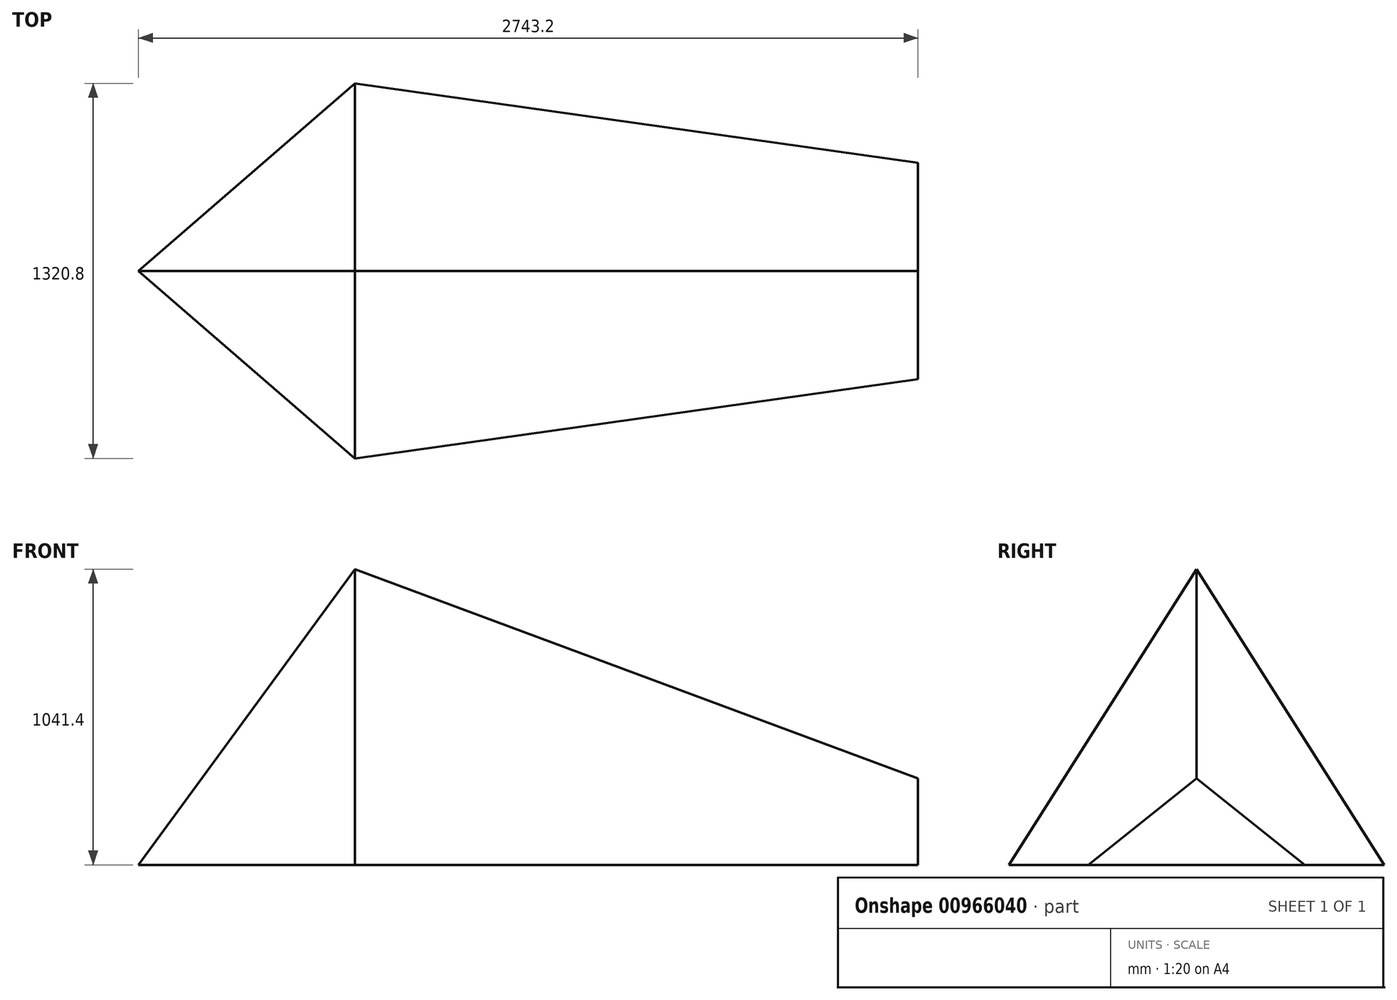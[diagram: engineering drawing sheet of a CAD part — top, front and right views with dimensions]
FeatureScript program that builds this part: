
annotation { "Feature Type Name" : "Feature", "Feature Type Description" : "" }
export const myFeature = defineFeature(function(context is Context, id is Id, definition is map)
    precondition{}
    {
        {
            var Q0;
            Q0=qCreatedBy(makeId("Top.planeOp"),FACE);
            var sketch = newSketch(context, id + "F0", { "sketchPlane" : qUnion([Q0])});
            skLineSegment(sketch, "E0.bottom", {"start": v(914.4, 254) * mm, "end": v(-914.4, 254) * mm});
            skLineSegment(sketch, "E0.top", {"start": v(914.4, -254) * mm, "end": v(-914.4, -254) * mm});
            skLineSegment(sketch, "E0.left", {"start": v(914.4, 254) * mm, "end": v(914.4, -254) * mm});
            skLineSegment(sketch, "E0.right", {"start": v(-914.4, 254) * mm, "end": v(-914.4, -254) * mm});
            skPoint(sketch, "E0.middle", {"position": v(0, 0) * mm});
            skSolve(sketch);
        }
        {
            var Q0;
            Q0=qCreatedBy(makeId("Top.planeOp"),FACE);
            var sketch = newSketch(context, id + "F1", { "sketchPlane" : qUnion([Q0])});
            skLineSegment(sketch, "E1", {"start": v(-914.4, 660.4) * mm, "end": v(-914.4, -660.4) * mm, "construction": true});
            skPoint(sketch, "E2", {"position": v(-914.4, 0) * mm});
            skLineSegment(sketch, "E3", {"start": v(-1676.4, 0) * mm, "end": v(1066.8, 0) * mm, "construction": true});
            skLineSegment(sketch, "E4", {"start": v(1066.8, 381) * mm, "end": v(1066.8, -381) * mm, "construction": true});
            skLineSegment(sketch, "E5", {"start": v(-1676.4, 0) * mm, "end": v(-914.4, 660.4) * mm, "construction": true});
            skLineSegment(sketch, "E6", {"start": v(-914.4, 660.4) * mm, "end": v(1066.8, 381) * mm, "construction": true});
            skLineSegment(sketch, "E7", {"start": v(1066.8, -381) * mm, "end": v(-914.4, -660.4) * mm, "construction": true});
            skLineSegment(sketch, "E8", {"start": v(-1676.4, 0) * mm, "end": v(-914.4, -660.4) * mm, "construction": true});
            skSolve(sketch);
        }
        {
            var Q0;
            Q0=qCreatedBy(makeId("Front.planeOp"),FACE);
            var sketch = newSketch(context, id + "F2", { "sketchPlane" : qUnion([Q0])});
            skPoint(sketch, "E9.0", {"position": v(-914.4, 0) * mm});
            skPoint(sketch, "E10.0", {"position": v(-1676.4, 0) * mm});
            skPoint(sketch, "E11.0", {"position": v(1066.8, 0) * mm});
            skLineSegment(sketch, "E12", {"start": v(-914.4, 0) * mm, "end": v(-914.4, 1041.4) * mm, "construction": true});
            skLineSegment(sketch, "E13", {"start": v(-914.4, 1041.4) * mm, "end": v(-1676.4, 0) * mm, "construction": true});
            skLineSegment(sketch, "E14", {"start": v(1066.8, 0) * mm, "end": v(1066.8, 304.8) * mm, "construction": true});
            skLineSegment(sketch, "E15", {"start": v(1066.8, 304.8) * mm, "end": v(-914.4, 1041.4) * mm, "construction": true});
            skSolve(sketch);
        }
        {
            var Q0;
            Q0=sQuery(id+"F1.wireOp",EDGE,"E1");
            var Q1;
            Q1=sQuery(id+"F2.wireOp",EDGE,"E12");
            cPlane(context, id + "F3", {"entities" : qUnion([Q0, Q1]), "cplaneType" : CPlaneType.LINE_ANGLE, "offset" : 25.4 * mm, "angle" : 0 * degree, "width" : 152.4 * mm, "height" : 152.4 * mm});
        }
        {
            var Q0;
            Q0=sQuery(id+"F1.wireOp",EDGE,"E4");
            var Q1;
            Q1=sQuery(id+"F2.wireOp",EDGE,"E14");
            cPlane(context, id + "F4", {"entities" : qUnion([Q0, Q1]), "cplaneType" : CPlaneType.LINE_ANGLE, "offset" : 25.4 * mm, "angle" : 0 * degree, "width" : 152.4 * mm, "height" : 152.4 * mm});
        }
        {
            var Q0;
            Q0=qCreatedBy(id+"F3.planeOp",FACE);
            var sketch = newSketch(context, id + "F5", { "sketchPlane" : qUnion([Q0])});
            skPoint(sketch, "E16.0", {"position": v(-660.4, 0) * mm});
            skPoint(sketch, "E17.0", {"position": v(660.4, 0) * mm});
            skPoint(sketch, "E18.0", {"position": v(0, 1041.4) * mm});
            skLineSegment(sketch, "E19", {"start": v(-660.4, 0) * mm, "end": v(660.4, 0) * mm});
            skLineSegment(sketch, "E20", {"start": v(0, 1041.4) * mm, "end": v(660.4, 0) * mm});
            skLineSegment(sketch, "E21", {"start": v(-660.4, 0) * mm, "end": v(0, 1041.4) * mm});
            skSolve(sketch);
        }
        {
            var Q0;
            Q0=qCreatedBy(id+"F4.planeOp",FACE);
            var sketch = newSketch(context, id + "F6", { "sketchPlane" : qUnion([Q0])});
            skPoint(sketch, "E22.0", {"position": v(-381, 0) * mm});
            skPoint(sketch, "E23.0", {"position": v(381, 0) * mm});
            skPoint(sketch, "E24.0", {"position": v(0, 304.8) * mm});
            skLineSegment(sketch, "E25", {"start": v(-381, 0) * mm, "end": v(381, 0) * mm});
            skLineSegment(sketch, "E26", {"start": v(381, 0) * mm, "end": v(0, 304.8) * mm});
            skLineSegment(sketch, "E27", {"start": v(0, 304.8) * mm, "end": v(-381, 0) * mm});
            skSolve(sketch);
        }
        {
            var Q0;
            Q0=makeQuery(id+"F6.imprint","IMPRINT",FACE,{"disambiguationData":[TD([[makeQuery(id+"F6.imprint","IMPRINT",EDGE,{"derivedFrom":sQuery(id+"F6.wireOp",EDGE,"E25")}),1.0]])]});
            var Q1;
            Q1=makeQuery(id+"F5.imprint","IMPRINT",FACE,{"disambiguationData":[TD([[makeQuery(id+"F5.imprint","IMPRINT",EDGE,{"derivedFrom":sQuery(id+"F5.wireOp",EDGE,"E19")}),1.0]])]});
            loft(context, id + "F7", {"sheetProfilesArray" : [{ "sheetProfileEntities" : qUnion([Q0]) }, { "sheetProfileEntities" : qUnion([Q1]) }]});
        }
        {
            var Q1;
            Q1=makeQuery(id+"F7.opLoft","CAP_FACE",FACE,{"disambiguationData":[OSD([makeQuery(id+"F5.imprint","IMPRINT",FACE,{"disambiguationData":[TD([[makeQuery(id+"F5.imprint","IMPRINT",EDGE,{"derivedFrom":sQuery(id+"F5.wireOp",EDGE,"E19")}),1.0]])]})])],"isStart":true});
            var Q2;
            Q2=sQuery(id+"F2.wireOp",VERTEX,"E10.0");
            loft(context, id + "F8", {"operationType" : NewBodyOperationType.ADD, "sheetProfilesArray" : [{ "sheetProfileEntities" : qUnion([Q1]) }, { "sheetProfileEntities" : qUnion([Q2]) }]});
        }
    });
